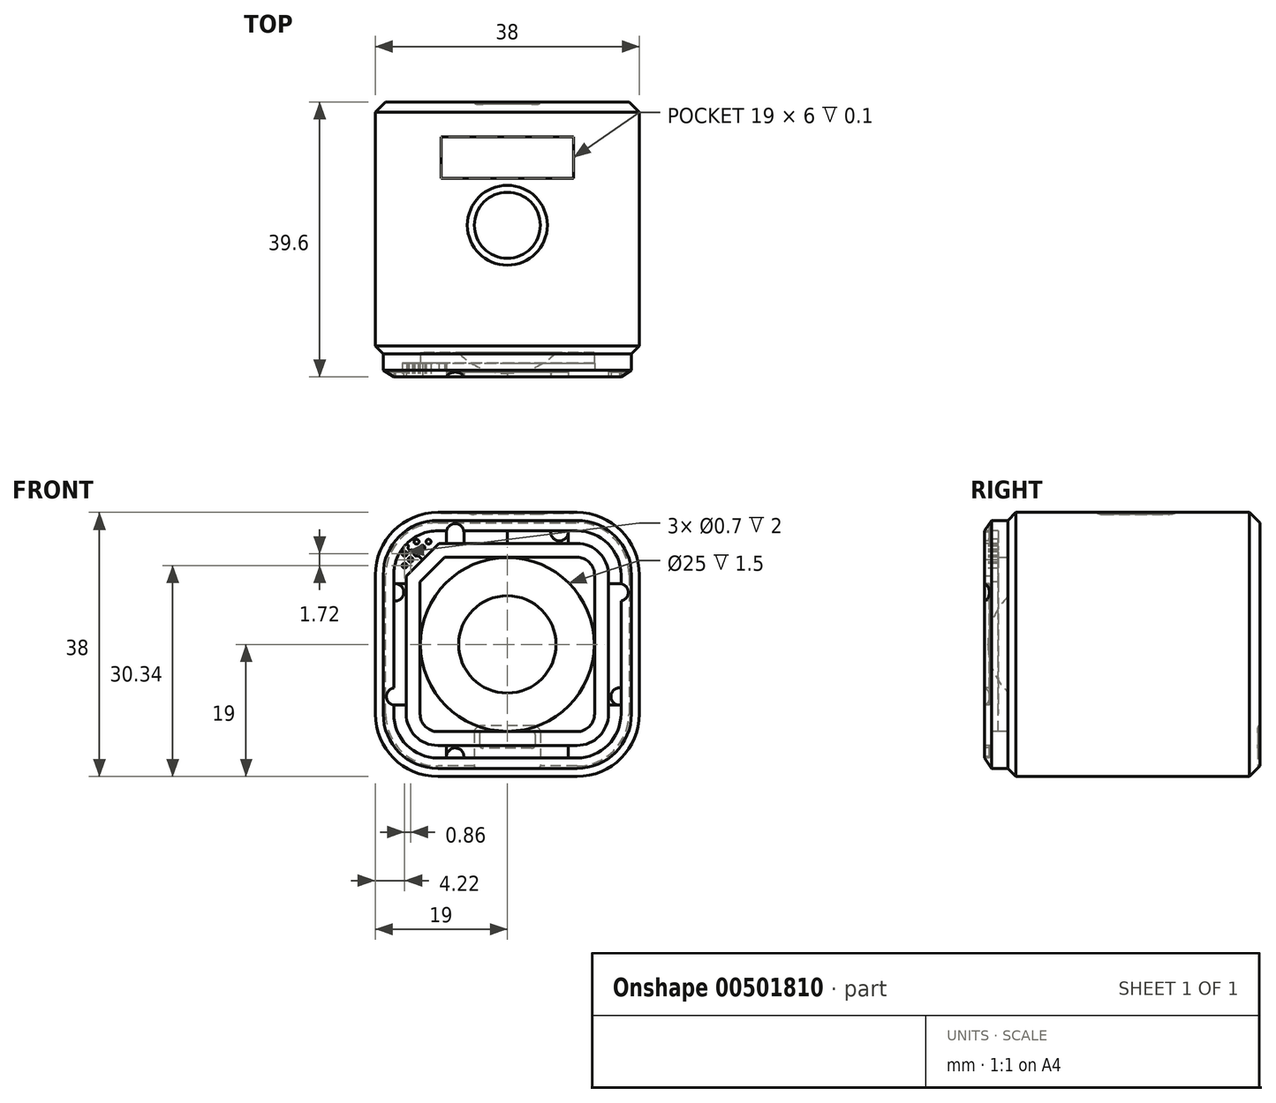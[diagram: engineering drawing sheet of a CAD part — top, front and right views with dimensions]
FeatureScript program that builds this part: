
annotation { "Feature Type Name" : "Feature", "Feature Type Description" : "" }
export const myFeature = defineFeature(function(context is Context, id is Id, definition is map)
    precondition{}
    {
        {
            var Q0;
            Q0=qCreatedBy(makeId("Front.planeOp"),FACE);
            var sketch = newSketch(context, id + "F0", { "sketchPlane" : qUnion([Q0])});
            skLineSegment(sketch, "E0.bottom", {"start": v(19, 19) * mm, "end": v(-19, 19) * mm});
            skLineSegment(sketch, "E0.top", {"start": v(19, -19) * mm, "end": v(-19, -19) * mm});
            skLineSegment(sketch, "E0.left", {"start": v(19, 19) * mm, "end": v(19, -19) * mm});
            skLineSegment(sketch, "E0.right", {"start": v(-19, 19) * mm, "end": v(-19, -19) * mm});
            skPoint(sketch, "E0.middle", {"position": v(0, 0) * mm});
            skLineSegment(sketch, "E1.0", {"start": v(17.85, 17.85) * mm, "end": v(-17.85, 17.85) * mm});
            skLineSegment(sketch, "E1.1", {"start": v(17.85, 17.85) * mm, "end": v(17.85, -17.85) * mm});
            skLineSegment(sketch, "E1.2", {"start": v(17.85, -17.85) * mm, "end": v(-17.85, -17.85) * mm});
            skLineSegment(sketch, "E1.3", {"start": v(-17.85, 17.85) * mm, "end": v(-17.85, -17.85) * mm});
            skSolve(sketch);
        }
        {
            var Q0;
            Q0=makeQuery(id+"F0.imprint","IMPRINT",FACE,{"disambiguationData":[TD([[makeQuery(id+"F0.imprint","IMPRINT",EDGE,{"derivedFrom":sQuery(id+"F0.wireOp",EDGE,"E0.bottom")}),1.0]])]});
            var Q1;
            Q1=makeQuery(id+"F0.imprint","IMPRINT",FACE,{"disambiguationData":[TD([[makeQuery(id+"F0.imprint","IMPRINT",EDGE,{"derivedFrom":sQuery(id+"F0.wireOp",EDGE,"E1.0")}),1.0]])]});
            extrude(context, id + "F1", {"entities" : qUnion([Q0, Q1]), "oppositeDirection" : true, "depth" : 36.6 * mm});
        }
        {
            var Q0;
            Q0=makeQuery(id+"F1.opExtrude","SWEPT_EDGE",EDGE,{"disambiguationData":[OSD([sQuery(id+"F0.wireOp",EDGE,"E0.bottom"),sQuery(id+"F0.wireOp",EDGE,"E0.left")])]});
            var Q1;
            Q1=makeQuery(id+"F1.opExtrude","SWEPT_EDGE",EDGE,{"disambiguationData":[OSD([sQuery(id+"F0.wireOp",EDGE,"E0.bottom"),sQuery(id+"F0.wireOp",EDGE,"E0.right")])]});
            var Q2;
            Q2=makeQuery(id+"F1.opExtrude","SWEPT_EDGE",EDGE,{"disambiguationData":[OSD([sQuery(id+"F0.wireOp",EDGE,"E0.top"),sQuery(id+"F0.wireOp",EDGE,"E0.left")])]});
            var Q3;
            Q3=makeQuery(id+"F1.opExtrude","SWEPT_EDGE",EDGE,{"disambiguationData":[OSD([sQuery(id+"F0.wireOp",EDGE,"E0.top"),sQuery(id+"F0.wireOp",EDGE,"E0.right")])]});
            fillet(context, id + "F2", {"entities" : qUnion([Q0, Q1, Q2, Q3]), "radius" : 9 * mm, "tangentPropagation" : true, "allowEdgeOverflow" : false});
        }
        {
            var Q0;
            Q0=makeQuery(id+"F0.imprint","IMPRINT",FACE,{"disambiguationData":[TD([[makeQuery(id+"F0.imprint","IMPRINT",EDGE,{"derivedFrom":sQuery(id+"F0.wireOp",EDGE,"E1.0")}),1.0]])]});
            extrude(context, id + "F3", {"entities" : qUnion([Q0]), "operationType" : NewBodyOperationType.ADD, "depth" : 3 * mm});
        }
        {
            var Q0;
            Q0=makeQuery(id+"F3.opExtrude","SWEPT_EDGE",EDGE,{"disambiguationData":[OSD([sQuery(id+"F0.wireOp",EDGE,"E1.0"),sQuery(id+"F0.wireOp",EDGE,"E1.1")])]});
            var Q1;
            Q1=makeQuery(id+"F3.opExtrude","SWEPT_EDGE",EDGE,{"disambiguationData":[OSD([sQuery(id+"F0.wireOp",EDGE,"E1.0"),sQuery(id+"F0.wireOp",EDGE,"E1.3")])]});
            var Q2;
            Q2=makeQuery(id+"F3.opExtrude","SWEPT_EDGE",EDGE,{"disambiguationData":[OSD([sQuery(id+"F0.wireOp",EDGE,"E1.2"),sQuery(id+"F0.wireOp",EDGE,"E1.3")])]});
            var Q3;
            Q3=makeQuery(id+"F3.opExtrude","SWEPT_EDGE",EDGE,{"disambiguationData":[OSD([sQuery(id+"F0.wireOp",EDGE,"E1.1"),sQuery(id+"F0.wireOp",EDGE,"E1.2")])]});
            fillet(context, id + "F4", {"entities" : qUnion([Q0, Q1, Q2, Q3]), "radius" : 7.85 * mm, "tangentPropagation" : true, "allowEdgeOverflow" : false});
        }
        {
            var Q0;
            Q0=makeQuery(id+"F1.opExtrude","SWEPT_FACE",FACE,{"disambiguationData":[OSD([sQuery(id+"F0.wireOp",EDGE,"E0.bottom")])]});
            var sketch = newSketch(context, id + "F5", { "sketchPlane" : qUnion([Q0])});
            skCircle(sketch, "E2", {"center": v(0, 18.85) * mm, "radius": 5.75 * mm});
            skCircle(sketch, "E3.0", {"center": v(0, 18.85) * mm, "radius": 4.75 * mm});
            skLineSegment(sketch, "E4.bottom", {"start": v(-9.5, 31.6) * mm, "end": v(9.5, 31.6) * mm});
            skLineSegment(sketch, "E4.top", {"start": v(-9.5, 25.6) * mm, "end": v(9.5, 25.6) * mm});
            skLineSegment(sketch, "E4.left", {"start": v(-9.5, 31.6) * mm, "end": v(-9.5, 25.6) * mm});
            skLineSegment(sketch, "E4.right", {"start": v(9.5, 31.6) * mm, "end": v(9.5, 25.6) * mm});
            skPoint(sketch, "E4.middle", {"position": v(0, 28.6) * mm});
            skSolve(sketch);
        }
        {
            var Q0;
            Q0=makeQuery(id+"F5.imprint","IMPRINT",FACE,{"disambiguationData":[TD([[makeQuery(id+"F5.imprint","IMPRINT",EDGE,{"derivedFrom":sQuery(id+"F5.wireOp",EDGE,"E2")}),1.0]])]});
            extrude(context, id + "F6", {"entities" : qUnion([Q0]), "operationType" : NewBodyOperationType.REMOVE, "oppositeDirection" : true, "depth" : 0.3 * mm});
        }
        {
            var Q0;
            Q0=makeQuery(id+"F6.boolean.opBoolean","COPY",EDGE,{"derivedFrom":makeQuery(id+"F6.opExtrude","CAP_EDGE",EDGE,{"disambiguationData":[OSD([sQuery(id+"F5.wireOp",EDGE,"E3.0")])],"isStart":true})});
            fillet(context, id + "F7", {"entities" : qUnion([Q0]), "radius" : 0.1 * mm, "tangentPropagation" : true, "allowEdgeOverflow" : false});
        }
        {
            var Q0;
            Q0=makeQuery(id+"F5.imprint","IMPRINT",FACE,{"disambiguationData":[TD([[makeQuery(id+"F5.imprint","IMPRINT",EDGE,{"derivedFrom":sQuery(id+"F5.wireOp",EDGE,"E4.bottom")}),-1.0]])]});
            extrude(context, id + "F8", {"entities" : qUnion([Q0]), "operationType" : NewBodyOperationType.REMOVE, "oppositeDirection" : true, "depth" : 0.1 * mm});
        }
        {
            var Q0;
            Q0=makeQuery(id+"F6.boolean.opBoolean","COPY",EDGE,{"derivedFrom":makeQuery(id+"F6.opExtrude","CAP_EDGE",EDGE,{"disambiguationData":[OSD([sQuery(id+"F5.wireOp",EDGE,"E2")])],"isStart":false})});
            fillet(context, id + "F9", {"entities" : qUnion([Q0]), "radius" : 1.7 * mm, "tangentPropagation" : true, "allowEdgeOverflow" : false});
        }
        {
            var Q0;
            Q0=makeQuery(id+"F1.opExtrude","CAP_FACE",FACE,{"disambiguationData":[OSD([sQuery(id+"F0.wireOp",EDGE,"E0.bottom"),sQuery(id+"F0.wireOp",EDGE,"E0.top"),sQuery(id+"F0.wireOp",EDGE,"E0.left"),sQuery(id+"F0.wireOp",EDGE,"E0.right")])],"isStart":false});
            var Q1;
            Q1=makeQuery(id+"F1.opExtrude","CAP_EDGE",EDGE,{"disambiguationData":[OSD([sQuery(id+"F0.wireOp",EDGE,"E0.bottom")])],"isStart":true});
            chamfer(context, id + "F10", {"entities" : qUnion([Q0, Q1]), "width" : 1.5 * mm, "tangentPropagation" : true});
        }
        {
            var Q0;
            Q0=makeQuery(id+"F3.opExtrude","CAP_FACE",FACE,{"disambiguationData":[OSD([sQuery(id+"F0.wireOp",EDGE,"E1.0"),sQuery(id+"F0.wireOp",EDGE,"E1.1"),sQuery(id+"F0.wireOp",EDGE,"E1.2"),sQuery(id+"F0.wireOp",EDGE,"E1.3")])],"isStart":false});
            chamfer(context, id + "F11", {"entities" : qUnion([Q0]), "chamferType" : ChamferType.TWO_OFFSETS, "width1" : 1.5 * mm, "oppositeDirection" : false, "width2" : 1 * mm, "tangentPropagation" : true});
        }
        {
            var Q0;
            Q0=makeQuery(id+"F3.opExtrude","CAP_FACE",FACE,{"disambiguationData":[OSD([sQuery(id+"F0.wireOp",EDGE,"E1.0"),sQuery(id+"F0.wireOp",EDGE,"E1.1"),sQuery(id+"F0.wireOp",EDGE,"E1.2"),sQuery(id+"F0.wireOp",EDGE,"E1.3")])],"isStart":false});
            var sketch = newSketch(context, id + "F12", { "sketchPlane" : qUnion([Q0])});
            skLineSegment(sketch, "E5.1", {"start": v(10, 14.55) * mm, "end": v(-9.85, 14.55) * mm});
            skLineSegment(sketch, "E5.2", {"start": v(-14.55, 9.85) * mm, "end": v(-14.55, -10) * mm});
            skArc(sketch, "E5.3", {"start": v(14.55, 10) * mm, "mid": v(13.22, 13.22) * mm, "end": v(10, 14.55) * mm});
            skArc(sketch, "E5.4", {"start": v(-14.55, -10) * mm, "mid": v(-13.22, -13.22) * mm, "end": v(-10, -14.55) * mm});
            skLineSegment(sketch, "E5.5", {"start": v(-10, -14.55) * mm, "end": v(10, -14.55) * mm});
            skArc(sketch, "E5.6", {"start": v(10, -14.55) * mm, "mid": v(13.22, -13.22) * mm, "end": v(14.55, -10) * mm});
            skLineSegment(sketch, "E5.7", {"start": v(14.55, -10) * mm, "end": v(14.55, 10) * mm});
            skLineSegment(sketch, "E6", {"start": v(-14.55, 9.85) * mm, "end": v(-9.85, 14.55) * mm});
            skCircle(sketch, "E7", {"center": v(-13.06, 13.06) * mm, "radius": 0.35 * mm});
            skLineSegment(sketch, "E8", {"start": v(-12.2, 12.2) * mm, "end": v(-14.5, 14.5) * mm});
            skCircle(sketch, "E9", {"center": v(-13.92, 13.92) * mm, "radius": 0.35 * mm});
            skCircle(sketch, "E10", {"center": v(-13.92, 12.2) * mm, "radius": 0.35 * mm});
            skCircle(sketch, "E11", {"center": v(-14.78, 11.34) * mm, "radius": 0.35 * mm});
            skCircle(sketch, "E12", {"center": v(-14.78, 13.06) * mm, "radius": 0.35 * mm});
            skCircle(sketch, "E13.MirrorC", {"center": v(-12.2, 13.92) * mm, "radius": 0.35 * mm});
            skCircle(sketch, "E14.MirrorC", {"center": v(-13.06, 14.78) * mm, "radius": 0.35 * mm});
            skCircle(sketch, "E15.MirrorC", {"center": v(-11.34, 14.78) * mm, "radius": 0.35 * mm});
            skPoint(sketch, "E16", {"position": v(-7.5, 16.15) * mm});
            skLineSegment(sketch, "E17", {"start": v(0, 16.35) * mm, "end": v(0, 14.55) * mm});
            skCircle(sketch, "E18", {"center": v(-7.5, 16.15) * mm, "radius": 1.25 * mm});
            skLineSegment(sketch, "E19", {"start": v(-8.75, 16.15) * mm, "end": v(-8.75, 14.55) * mm});
            skLineSegment(sketch, "E20", {"start": v(-6.25, 16.15) * mm, "end": v(-6.25, 14.55) * mm});
            skLineSegment(sketch, "E21.MirrorCS", {"start": v(6.25, 16.15) * mm, "end": v(6.25, 14.55) * mm});
            skCircle(sketch, "E22.MirrorC", {"center": v(7.5, 16.15) * mm, "radius": 1.25 * mm});
            skLineSegment(sketch, "E23.MirrorCS", {"start": v(8.75, 16.15) * mm, "end": v(8.75, 14.55) * mm});
            skLineSegment(sketch, "E24.MirrorCS", {"start": v(-6.25, -16.15) * mm, "end": v(-6.25, -14.55) * mm});
            skCircle(sketch, "E25.MirrorC", {"center": v(-7.5, -16.15) * mm, "radius": 1.25 * mm});
            skLineSegment(sketch, "E26.MirrorCS", {"start": v(-8.75, -16.15) * mm, "end": v(-8.75, -14.55) * mm});
            skLineSegment(sketch, "E27.MirrorCS", {"start": v(6.25, -16.15) * mm, "end": v(6.25, -14.55) * mm});
            skCircle(sketch, "E28.MirrorC", {"center": v(7.5, -16.15) * mm, "radius": 1.25 * mm});
            skLineSegment(sketch, "E29.MirrorCS", {"start": v(8.75, -16.15) * mm, "end": v(8.75, -14.55) * mm});
            skLineSegment(sketch, "E30.MirrorCS", {"start": v(-16.15, -8.75) * mm, "end": v(-14.55, -8.75) * mm});
            skCircle(sketch, "E31.MirrorC", {"center": v(-16.15, -7.5) * mm, "radius": 1.25 * mm});
            skLineSegment(sketch, "E32.MirrorCS", {"start": v(-16.15, -6.25) * mm, "end": v(-14.55, -6.25) * mm});
            skLineSegment(sketch, "E33.MirrorCS", {"start": v(-16.15, 6.25) * mm, "end": v(-14.55, 6.25) * mm});
            skCircle(sketch, "E34.MirrorC", {"center": v(-16.15, 7.5) * mm, "radius": 1.25 * mm});
            skLineSegment(sketch, "E35.MirrorCS", {"start": v(-16.15, 8.75) * mm, "end": v(-14.55, 8.75) * mm});
            skLineSegment(sketch, "E36.MirrorCS", {"start": v(16.15, 8.75) * mm, "end": v(14.55, 8.75) * mm});
            skCircle(sketch, "E37.MirrorC", {"center": v(16.15, 7.5) * mm, "radius": 1.25 * mm});
            skLineSegment(sketch, "E38.MirrorCS", {"start": v(16.15, 6.25) * mm, "end": v(14.55, 6.25) * mm});
            skLineSegment(sketch, "E39.MirrorCS", {"start": v(16.15, -6.25) * mm, "end": v(14.55, -6.25) * mm});
            skCircle(sketch, "E40.MirrorC", {"center": v(16.15, -7.5) * mm, "radius": 1.25 * mm});
            skLineSegment(sketch, "E41.MirrorCS", {"start": v(16.15, -8.75) * mm, "end": v(14.55, -8.75) * mm});
            skSolve(sketch);
        }
        {
            var Q0;
            Q0=makeQuery(id+"F12.imprint","IMPRINT",FACE,{"disambiguationData":[TD([[makeQuery(id+"F12.imprint","IMPRINT",EDGE,{"derivedFrom":sQuery(id+"F12.wireOp",EDGE,"E5.1")}),1.0]])]});
            extrude(context, id + "F13", {"entities" : qUnion([Q0]), "operationType" : NewBodyOperationType.REMOVE, "oppositeDirection" : true, "depth" : 1 * mm});
        }
        {
            var Q0;
            Q0=makeQuery(id+"F13.boolean.opBoolean","COPY",FACE,{"derivedFrom":makeQuery(id+"F13.opExtrude","CAP_FACE",FACE,{"disambiguationData":[OSD([sQuery(id+"F12.wireOp",EDGE,"E5.1"),sQuery(id+"F12.wireOp",EDGE,"E5.2"),sQuery(id+"F12.wireOp",EDGE,"E5.3"),sQuery(id+"F12.wireOp",EDGE,"E5.4"),sQuery(id+"F12.wireOp",EDGE,"E5.5"),sQuery(id+"F12.wireOp",EDGE,"E5.6"),sQuery(id+"F12.wireOp",EDGE,"E5.7"),sQuery(id+"F12.wireOp",EDGE,"E6")])],"isStart":false})});
            var sketch = newSketch(context, id + "F14", { "sketchPlane" : qUnion([Q0])});
            skLineSegment(sketch, "E42.0", {"start": v(12.55, -10) * mm, "end": v(12.55, 10) * mm});
            skArc(sketch, "E42.1", {"start": v(10, -12.55) * mm, "mid": v(11.8, -11.8) * mm, "end": v(12.55, -10) * mm});
            skArc(sketch, "E42.2", {"start": v(12.55, 10) * mm, "mid": v(11.8, 11.8) * mm, "end": v(10, 12.55) * mm});
            skLineSegment(sketch, "E42.3", {"start": v(-10, -12.55) * mm, "end": v(10, -12.55) * mm});
            skLineSegment(sketch, "E42.4", {"start": v(10, 12.55) * mm, "end": v(-9.02, 12.55) * mm});
            skLineSegment(sketch, "E42.5", {"start": v(-9.02, 12.55) * mm, "end": v(-12.55, 9.02) * mm});
            skLineSegment(sketch, "E42.6", {"start": v(-12.55, 9.02) * mm, "end": v(-12.55, -10) * mm});
            skArc(sketch, "E42.7", {"start": v(-12.55, -10) * mm, "mid": v(-11.8, -11.8) * mm, "end": v(-10, -12.55) * mm});
            skCircle(sketch, "E43", {"center": v(0, 0) * mm, "radius": 12.5 * mm});
            skPoint(sketch, "E44", {"position": v(0, -12.55) * mm});
            skPoint(sketch, "E45", {"position": v(12.55, 0) * mm});
            skSolve(sketch);
        }
        {
            var Q0;
            Q0=makeQuery(id+"F14.imprint","IMPRINT",FACE,{"disambiguationData":[TD([[makeQuery(id+"F14.imprint","IMPRINT",EDGE,{"derivedFrom":sQuery(id+"F14.wireOp",EDGE,"E42.0")}),1.0]])]});
            extrude(context, id + "F15", {"entities" : qUnion([Q0]), "operationType" : NewBodyOperationType.REMOVE, "oppositeDirection" : true, "depth" : 1 * mm});
        }
        {
            var Q0;
            Q0=makeQuery(id+"F15.boolean.opBoolean","SPLIT",FACE,{"disambiguationData":[TD([makeQuery(id+"F15.opExtrude","SWEPT_FACE",FACE,{"disambiguationData":[OSD([sQuery(id+"F14.wireOp",EDGE,"E43")])]})])],"derivedFrom":makeQuery(id+"F13.boolean.opBoolean","COPY",FACE,{"derivedFrom":makeQuery(id+"F13.opExtrude","CAP_FACE",FACE,{"disambiguationData":[OSD([sQuery(id+"F12.wireOp",EDGE,"E5.1"),sQuery(id+"F12.wireOp",EDGE,"E5.2"),sQuery(id+"F12.wireOp",EDGE,"E5.3"),sQuery(id+"F12.wireOp",EDGE,"E5.4"),sQuery(id+"F12.wireOp",EDGE,"E5.5"),sQuery(id+"F12.wireOp",EDGE,"E5.6"),sQuery(id+"F12.wireOp",EDGE,"E5.7"),sQuery(id+"F12.wireOp",EDGE,"E6")])],"isStart":false})})});
            extrude(context, id + "F16", {"entities" : qUnion([Q0]), "operationType" : NewBodyOperationType.REMOVE, "oppositeDirection" : true, "depth" : 2.5 * mm});
        }
        {
            var Q0;
            Q0=makeQuery(id+"F16.boolean.opBoolean","COPY",FACE,{"derivedFrom":makeQuery(id+"F16.opExtrude","CAP_FACE",FACE,{"disambiguationData":[OSD([sQuery(id+"F12.wireOp",EDGE,"E5.1"),sQuery(id+"F12.wireOp",EDGE,"E5.2"),sQuery(id+"F12.wireOp",EDGE,"E5.3"),sQuery(id+"F12.wireOp",EDGE,"E5.4"),sQuery(id+"F12.wireOp",EDGE,"E5.5"),sQuery(id+"F12.wireOp",EDGE,"E5.6"),sQuery(id+"F12.wireOp",EDGE,"E5.7"),sQuery(id+"F12.wireOp",EDGE,"E6")])],"isStart":false})});
            var sketch = newSketch(context, id + "F17", { "sketchPlane" : qUnion([Q0])});
            skCircle(sketch, "E46.0", {"center": v(0, 0) * mm, "radius": 7 * mm});
            skCircle(sketch, "E47.0", {"center": v(0, 0) * mm, "radius": 17.5 * mm});
            skSolve(sketch);
        }
        {
            var Q0;
            Q0=makeQuery(id+"F17.imprint","IMPRINT",FACE,{"disambiguationData":[TD([[makeQuery(id+"F17.imprint","IMPRINT",EDGE,{"derivedFrom":sQuery(id+"F17.wireOp",EDGE,"E46.0")}),1.0]])]});
            extrude(context, id + "F18", {"entities" : qUnion([Q0]), "operationType" : NewBodyOperationType.ADD, "depth" : 3 * mm});
        }
        {
            var Q0;
            Q0=makeQuery(id+"F18.opExtrude","CAP_EDGE",EDGE,{"disambiguationData":[OSD([sQuery(id+"F17.wireOp",EDGE,"E46.0")])],"isStart":false});
            fillet(context, id + "F19", {"entities" : qUnion([Q0]), "radius" : 9.5 * mm, "tangentPropagation" : true, "allowEdgeOverflow" : false});
        }
        {
            var Q0;
            Q0=makeQuery(id+"F12.imprint","IMPRINT",FACE,{"disambiguationData":[TD([[makeQuery(id+"F12.imprint","IMPRINT",EDGE,{"derivedFrom":sQuery(id+"F12.wireOp",EDGE,"E11")}),1.0]])]});
            var Q1;
            Q1=makeQuery(id+"F12.imprint","IMPRINT",FACE,{"disambiguationData":[TD([[makeQuery(id+"F12.imprint","IMPRINT",EDGE,{"derivedFrom":sQuery(id+"F12.wireOp",EDGE,"E10")}),1.0]])]});
            var Q2;
            Q2=makeQuery(id+"F12.imprint","IMPRINT",FACE,{"disambiguationData":[TD([[makeQuery(id+"F12.imprint","IMPRINT",EDGE,{"derivedFrom":sQuery(id+"F12.wireOp",EDGE,"E12")}),1.0]])]});
            var Q3;
            {var subQ0=sQuery(id+"F12.wireOp",EDGE,"E9");var subQ1=sQuery(id+"F12.wireOp",EDGE,"E8");var subQ2=makeQuery(id+"F12.imprint","INTERSECT",VERTEX,{"disambiguationData":[OD(0.0)],"derivedFrom":[subQ1,subQ0]});Q3=makeQuery(id+"F12.imprint","IMPRINT",FACE,{"disambiguationData":[TD([[makeQuery(id+"F12.imprint","IMPRINT",EDGE,{"disambiguationData":[TD([[subQ2,-1.0]])],"derivedFrom":subQ1}),1.0]])]});}
            var Q4;
            {var subQ0=sQuery(id+"F12.wireOp",EDGE,"E9");var subQ1=sQuery(id+"F12.wireOp",EDGE,"E8");var subQ2=makeQuery(id+"F12.imprint","INTERSECT",VERTEX,{"disambiguationData":[OD(0.0)],"derivedFrom":[subQ1,subQ0]});Q4=makeQuery(id+"F12.imprint","IMPRINT",FACE,{"disambiguationData":[TD([[makeQuery(id+"F12.imprint","IMPRINT",EDGE,{"disambiguationData":[TD([[subQ2,-1.0]])],"derivedFrom":subQ1}),-1.0]])]});}
            var Q5;
            Q5=makeQuery(id+"F12.imprint","IMPRINT",FACE,{"disambiguationData":[TD([[makeQuery(id+"F12.imprint","IMPRINT",EDGE,{"derivedFrom":sQuery(id+"F12.wireOp",EDGE,"E14.MirrorC")}),-1.0]])]});
            var Q6;
            {var subQ0=sQuery(id+"F12.wireOp",EDGE,"E8");var subQ1=sQuery(id+"F12.wireOp",EDGE,"E7");var subQ2=makeQuery(id+"F12.imprint","INTERSECT",VERTEX,{"disambiguationData":[OD(0.0)],"derivedFrom":[subQ1,subQ0]});Q6=makeQuery(id+"F12.imprint","IMPRINT",FACE,{"disambiguationData":[TD([[makeQuery(id+"F12.imprint","IMPRINT",EDGE,{"disambiguationData":[TD([[subQ2,1.0]])],"derivedFrom":subQ1}),1.0]])]});}
            var Q7;
            {var subQ0=sQuery(id+"F12.wireOp",EDGE,"E8");var subQ1=sQuery(id+"F12.wireOp",EDGE,"E7");var subQ2=makeQuery(id+"F12.imprint","INTERSECT",VERTEX,{"disambiguationData":[OD(0.0)],"derivedFrom":[subQ1,subQ0]});Q7=makeQuery(id+"F12.imprint","IMPRINT",FACE,{"disambiguationData":[TD([[makeQuery(id+"F12.imprint","IMPRINT",EDGE,{"disambiguationData":[TD([[subQ2,-1.0]])],"derivedFrom":subQ1}),1.0]])]});}
            var Q8;
            Q8=makeQuery(id+"F12.imprint","IMPRINT",FACE,{"disambiguationData":[TD([[makeQuery(id+"F12.imprint","IMPRINT",EDGE,{"derivedFrom":sQuery(id+"F12.wireOp",EDGE,"E15.MirrorC")}),-1.0]])]});
            var Q9;
            Q9=makeQuery(id+"F12.imprint","IMPRINT",FACE,{"disambiguationData":[TD([[makeQuery(id+"F12.imprint","IMPRINT",EDGE,{"derivedFrom":sQuery(id+"F12.wireOp",EDGE,"E13.MirrorC")}),-1.0]])]});
            extrude(context, id + "F20", {"entities" : qUnion([Q0, Q1, Q2, Q3, Q4, Q5, Q6, Q7, Q8, Q9]), "operationType" : NewBodyOperationType.REMOVE, "oppositeDirection" : true, "depth" : 2 * mm});
        }
        {
            var Q0;
            {var subQ0=sQuery(id+"F12.wireOp",EDGE,"E18");var subQ1=sQuery(id+"F0.wireOp",EDGE,"E1.0");var subQ2=makeQuery(id+"F11.opChamfer","BLEND_EDGE",EDGE,{"blendedFrom":[makeQuery(id+"F3.opExtrude","CAP_EDGE",EDGE,{"disambiguationData":[OSD([subQ1])],"isStart":false}),makeQuery(id+"F3.opExtrude","CAP_FACE",FACE,{"disambiguationData":[OSD([subQ1,sQuery(id+"F0.wireOp",EDGE,"E1.1"),sQuery(id+"F0.wireOp",EDGE,"E1.2"),sQuery(id+"F0.wireOp",EDGE,"E1.3")])],"isStart":false})],"blendedInto":[makeQuery(id+"F3.opExtrude","CAP_FACE",FACE,{"disambiguationData":[OSD([subQ1,sQuery(id+"F0.wireOp",EDGE,"E1.1"),sQuery(id+"F0.wireOp",EDGE,"E1.2"),sQuery(id+"F0.wireOp",EDGE,"E1.3")])],"isStart":false})]});var subQ3=makeQuery(id+"F12.imprint","INTERSECT",VERTEX,{"disambiguationData":[OD(0.0)],"derivedFrom":[subQ2,subQ0]});Q0=makeQuery(id+"F12.imprint","IMPRINT",FACE,{"disambiguationData":[TD([[makeQuery(id+"F12.imprint","IMPRINT",EDGE,{"disambiguationData":[TD([[subQ3,-1.0]])],"derivedFrom":subQ0}),1.0]])]});}
            var Q1;
            {var subQ0=sQuery(id+"F12.wireOp",EDGE,"E18");var subQ5=makeQuery(id+"F12.imprint","INTERSECT",VERTEX,{"derivedFrom":[subQ0,sQuery(id+"F12.wireOp",EDGE,"E19")]});Q1=makeQuery(id+"F12.imprint","IMPRINT",FACE,{"disambiguationData":[TD([[makeQuery(id+"F12.imprint","IMPRINT",EDGE,{"disambiguationData":[TD([[subQ5,-1.0]])],"derivedFrom":subQ0}),1.0]])]});}
            var Q2;
            {var subQ0=sQuery(id+"F12.wireOp",EDGE,"E19");Q2=makeQuery(id+"F12.imprint","IMPRINT",FACE,{"disambiguationData":[TD([[makeQuery(id+"F12.imprint","IMPRINT",EDGE,{"derivedFrom":subQ0}),1.0]])]});}
            var Q3;
            {var subQ0=sQuery(id+"F12.wireOp",EDGE,"E22.MirrorC");var subQ1=sQuery(id+"F0.wireOp",EDGE,"E1.0");var subQ2=makeQuery(id+"F11.opChamfer","BLEND_EDGE",EDGE,{"blendedFrom":[makeQuery(id+"F3.opExtrude","CAP_EDGE",EDGE,{"disambiguationData":[OSD([subQ1])],"isStart":false}),makeQuery(id+"F3.opExtrude","CAP_FACE",FACE,{"disambiguationData":[OSD([subQ1,sQuery(id+"F0.wireOp",EDGE,"E1.1"),sQuery(id+"F0.wireOp",EDGE,"E1.2"),sQuery(id+"F0.wireOp",EDGE,"E1.3")])],"isStart":false})],"blendedInto":[makeQuery(id+"F3.opExtrude","CAP_FACE",FACE,{"disambiguationData":[OSD([subQ1,sQuery(id+"F0.wireOp",EDGE,"E1.1"),sQuery(id+"F0.wireOp",EDGE,"E1.2"),sQuery(id+"F0.wireOp",EDGE,"E1.3")])],"isStart":false})]});var subQ3=makeQuery(id+"F12.imprint","INTERSECT",VERTEX,{"disambiguationData":[OD(0.0)],"derivedFrom":[subQ2,subQ0]});Q3=makeQuery(id+"F12.imprint","IMPRINT",FACE,{"disambiguationData":[TD([[makeQuery(id+"F12.imprint","IMPRINT",EDGE,{"disambiguationData":[TD([[subQ3,-1.0]])],"derivedFrom":subQ0}),-1.0]])]});}
            var Q4;
            {var subQ0=sQuery(id+"F12.wireOp",EDGE,"E22.MirrorC");var subQ1=makeQuery(id+"F12.imprint","INTERSECT",VERTEX,{"derivedFrom":[sQuery(id+"F12.wireOp",EDGE,"E21.MirrorCS"),subQ0]});Q4=makeQuery(id+"F12.imprint","IMPRINT",FACE,{"disambiguationData":[TD([[makeQuery(id+"F12.imprint","IMPRINT",EDGE,{"disambiguationData":[TD([[subQ1,1.0]])],"derivedFrom":subQ0}),-1.0]])]});}
            var Q5;
            {var subQ0=sQuery(id+"F12.wireOp",EDGE,"E21.MirrorCS");Q5=makeQuery(id+"F12.imprint","IMPRINT",FACE,{"disambiguationData":[TD([[makeQuery(id+"F12.imprint","IMPRINT",EDGE,{"derivedFrom":subQ0}),1.0]])]});}
            var Q6;
            {var subQ0=sQuery(id+"F12.wireOp",EDGE,"E36.MirrorCS");Q6=makeQuery(id+"F12.imprint","IMPRINT",FACE,{"disambiguationData":[TD([[makeQuery(id+"F12.imprint","IMPRINT",EDGE,{"derivedFrom":subQ0}),1.0]])]});}
            var Q7;
            {var subQ0=sQuery(id+"F12.wireOp",EDGE,"E37.MirrorC");var subQ5=makeQuery(id+"F12.imprint","INTERSECT",VERTEX,{"derivedFrom":[sQuery(id+"F12.wireOp",EDGE,"E36.MirrorCS"),subQ0]});Q7=makeQuery(id+"F12.imprint","IMPRINT",FACE,{"disambiguationData":[TD([[makeQuery(id+"F12.imprint","IMPRINT",EDGE,{"disambiguationData":[TD([[subQ5,-1.0]])],"derivedFrom":subQ0}),1.0]])]});}
            var Q8;
            {var subQ0=sQuery(id+"F12.wireOp",EDGE,"E37.MirrorC");var subQ1=sQuery(id+"F0.wireOp",EDGE,"E1.1");var subQ2=makeQuery(id+"F11.opChamfer","BLEND_EDGE",EDGE,{"blendedFrom":[makeQuery(id+"F3.opExtrude","CAP_EDGE",EDGE,{"disambiguationData":[OSD([subQ1])],"isStart":false}),makeQuery(id+"F3.opExtrude","CAP_FACE",FACE,{"disambiguationData":[OSD([sQuery(id+"F0.wireOp",EDGE,"E1.0"),subQ1,sQuery(id+"F0.wireOp",EDGE,"E1.2"),sQuery(id+"F0.wireOp",EDGE,"E1.3")])],"isStart":false})],"blendedInto":[makeQuery(id+"F3.opExtrude","CAP_FACE",FACE,{"disambiguationData":[OSD([sQuery(id+"F0.wireOp",EDGE,"E1.0"),subQ1,sQuery(id+"F0.wireOp",EDGE,"E1.2"),sQuery(id+"F0.wireOp",EDGE,"E1.3")])],"isStart":false})]});var subQ3=makeQuery(id+"F12.imprint","INTERSECT",VERTEX,{"disambiguationData":[OD(0.0)],"derivedFrom":[subQ2,subQ0]});Q8=makeQuery(id+"F12.imprint","IMPRINT",FACE,{"disambiguationData":[TD([[makeQuery(id+"F12.imprint","IMPRINT",EDGE,{"disambiguationData":[TD([[subQ3,-1.0]])],"derivedFrom":subQ0}),1.0]])]});}
            var Q9;
            {var subQ0=sQuery(id+"F12.wireOp",EDGE,"E39.MirrorCS");Q9=makeQuery(id+"F12.imprint","IMPRINT",FACE,{"disambiguationData":[TD([[makeQuery(id+"F12.imprint","IMPRINT",EDGE,{"derivedFrom":subQ0}),1.0]])]});}
            var Q10;
            {var subQ0=sQuery(id+"F12.wireOp",EDGE,"E40.MirrorC");var subQ1=makeQuery(id+"F12.imprint","INTERSECT",VERTEX,{"derivedFrom":[sQuery(id+"F12.wireOp",EDGE,"E39.MirrorCS"),subQ0]});Q10=makeQuery(id+"F12.imprint","IMPRINT",FACE,{"disambiguationData":[TD([[makeQuery(id+"F12.imprint","IMPRINT",EDGE,{"disambiguationData":[TD([[subQ1,1.0]])],"derivedFrom":subQ0}),-1.0]])]});}
            var Q11;
            {var subQ0=sQuery(id+"F12.wireOp",EDGE,"E40.MirrorC");var subQ1=sQuery(id+"F0.wireOp",EDGE,"E1.1");var subQ2=makeQuery(id+"F11.opChamfer","BLEND_EDGE",EDGE,{"blendedFrom":[makeQuery(id+"F3.opExtrude","CAP_EDGE",EDGE,{"disambiguationData":[OSD([subQ1])],"isStart":false}),makeQuery(id+"F3.opExtrude","CAP_FACE",FACE,{"disambiguationData":[OSD([sQuery(id+"F0.wireOp",EDGE,"E1.0"),subQ1,sQuery(id+"F0.wireOp",EDGE,"E1.2"),sQuery(id+"F0.wireOp",EDGE,"E1.3")])],"isStart":false})],"blendedInto":[makeQuery(id+"F3.opExtrude","CAP_FACE",FACE,{"disambiguationData":[OSD([sQuery(id+"F0.wireOp",EDGE,"E1.0"),subQ1,sQuery(id+"F0.wireOp",EDGE,"E1.2"),sQuery(id+"F0.wireOp",EDGE,"E1.3")])],"isStart":false})]});var subQ3=makeQuery(id+"F12.imprint","INTERSECT",VERTEX,{"disambiguationData":[OD(0.0)],"derivedFrom":[subQ2,subQ0]});Q11=makeQuery(id+"F12.imprint","IMPRINT",FACE,{"disambiguationData":[TD([[makeQuery(id+"F12.imprint","IMPRINT",EDGE,{"disambiguationData":[TD([[subQ3,-1.0]])],"derivedFrom":subQ0}),-1.0]])]});}
            var Q12;
            {var subQ0=sQuery(id+"F12.wireOp",EDGE,"E27.MirrorCS");Q12=makeQuery(id+"F12.imprint","IMPRINT",FACE,{"disambiguationData":[TD([[makeQuery(id+"F12.imprint","IMPRINT",EDGE,{"derivedFrom":subQ0}),-1.0]])]});}
            var Q13;
            {var subQ0=sQuery(id+"F12.wireOp",EDGE,"E28.MirrorC");var subQ1=makeQuery(id+"F12.imprint","INTERSECT",VERTEX,{"derivedFrom":[sQuery(id+"F12.wireOp",EDGE,"E27.MirrorCS"),subQ0]});Q13=makeQuery(id+"F12.imprint","IMPRINT",FACE,{"disambiguationData":[TD([[makeQuery(id+"F12.imprint","IMPRINT",EDGE,{"disambiguationData":[TD([[subQ1,1.0]])],"derivedFrom":subQ0}),1.0]])]});}
            var Q14;
            {var subQ0=sQuery(id+"F12.wireOp",EDGE,"E28.MirrorC");var subQ1=sQuery(id+"F0.wireOp",EDGE,"E1.2");var subQ2=makeQuery(id+"F11.opChamfer","BLEND_EDGE",EDGE,{"blendedFrom":[makeQuery(id+"F3.opExtrude","CAP_EDGE",EDGE,{"disambiguationData":[OSD([subQ1])],"isStart":false}),makeQuery(id+"F3.opExtrude","CAP_FACE",FACE,{"disambiguationData":[OSD([sQuery(id+"F0.wireOp",EDGE,"E1.0"),sQuery(id+"F0.wireOp",EDGE,"E1.1"),subQ1,sQuery(id+"F0.wireOp",EDGE,"E1.3")])],"isStart":false})],"blendedInto":[makeQuery(id+"F3.opExtrude","CAP_FACE",FACE,{"disambiguationData":[OSD([sQuery(id+"F0.wireOp",EDGE,"E1.0"),sQuery(id+"F0.wireOp",EDGE,"E1.1"),subQ1,sQuery(id+"F0.wireOp",EDGE,"E1.3")])],"isStart":false})]});var subQ3=makeQuery(id+"F12.imprint","INTERSECT",VERTEX,{"disambiguationData":[OD(0.0)],"derivedFrom":[subQ2,subQ0]});Q14=makeQuery(id+"F12.imprint","IMPRINT",FACE,{"disambiguationData":[TD([[makeQuery(id+"F12.imprint","IMPRINT",EDGE,{"disambiguationData":[TD([[subQ3,-1.0]])],"derivedFrom":subQ0}),1.0]])]});}
            var Q15;
            {var subQ0=sQuery(id+"F12.wireOp",EDGE,"E24.MirrorCS");Q15=makeQuery(id+"F12.imprint","IMPRINT",FACE,{"disambiguationData":[TD([[makeQuery(id+"F12.imprint","IMPRINT",EDGE,{"derivedFrom":subQ0}),1.0]])]});}
            var Q16;
            {var subQ0=sQuery(id+"F12.wireOp",EDGE,"E25.MirrorC");var subQ1=makeQuery(id+"F12.imprint","INTERSECT",VERTEX,{"derivedFrom":[sQuery(id+"F12.wireOp",EDGE,"E24.MirrorCS"),subQ0]});Q16=makeQuery(id+"F12.imprint","IMPRINT",FACE,{"disambiguationData":[TD([[makeQuery(id+"F12.imprint","IMPRINT",EDGE,{"disambiguationData":[TD([[subQ1,1.0]])],"derivedFrom":subQ0}),-1.0]])]});}
            var Q17;
            {var subQ0=sQuery(id+"F12.wireOp",EDGE,"E25.MirrorC");var subQ1=sQuery(id+"F0.wireOp",EDGE,"E1.2");var subQ2=makeQuery(id+"F11.opChamfer","BLEND_EDGE",EDGE,{"blendedFrom":[makeQuery(id+"F3.opExtrude","CAP_EDGE",EDGE,{"disambiguationData":[OSD([subQ1])],"isStart":false}),makeQuery(id+"F3.opExtrude","CAP_FACE",FACE,{"disambiguationData":[OSD([sQuery(id+"F0.wireOp",EDGE,"E1.0"),sQuery(id+"F0.wireOp",EDGE,"E1.1"),subQ1,sQuery(id+"F0.wireOp",EDGE,"E1.3")])],"isStart":false})],"blendedInto":[makeQuery(id+"F3.opExtrude","CAP_FACE",FACE,{"disambiguationData":[OSD([sQuery(id+"F0.wireOp",EDGE,"E1.0"),sQuery(id+"F0.wireOp",EDGE,"E1.1"),subQ1,sQuery(id+"F0.wireOp",EDGE,"E1.3")])],"isStart":false})]});var subQ3=makeQuery(id+"F12.imprint","INTERSECT",VERTEX,{"disambiguationData":[OD(0.0)],"derivedFrom":[subQ2,subQ0]});Q17=makeQuery(id+"F12.imprint","IMPRINT",FACE,{"disambiguationData":[TD([[makeQuery(id+"F12.imprint","IMPRINT",EDGE,{"disambiguationData":[TD([[subQ3,-1.0]])],"derivedFrom":subQ0}),-1.0]])]});}
            var Q18;
            {var subQ0=sQuery(id+"F12.wireOp",EDGE,"E34.MirrorC");var subQ1=sQuery(id+"F0.wireOp",EDGE,"E1.3");var subQ2=makeQuery(id+"F11.opChamfer","BLEND_EDGE",EDGE,{"blendedFrom":[makeQuery(id+"F3.opExtrude","CAP_EDGE",EDGE,{"disambiguationData":[OSD([subQ1])],"isStart":false}),makeQuery(id+"F3.opExtrude","CAP_FACE",FACE,{"disambiguationData":[OSD([sQuery(id+"F0.wireOp",EDGE,"E1.0"),sQuery(id+"F0.wireOp",EDGE,"E1.1"),sQuery(id+"F0.wireOp",EDGE,"E1.2"),subQ1])],"isStart":false})],"blendedInto":[makeQuery(id+"F3.opExtrude","CAP_FACE",FACE,{"disambiguationData":[OSD([sQuery(id+"F0.wireOp",EDGE,"E1.0"),sQuery(id+"F0.wireOp",EDGE,"E1.1"),sQuery(id+"F0.wireOp",EDGE,"E1.2"),subQ1])],"isStart":false})]});var subQ3=makeQuery(id+"F12.imprint","INTERSECT",VERTEX,{"disambiguationData":[OD(0.0)],"derivedFrom":[subQ2,subQ0]});Q18=makeQuery(id+"F12.imprint","IMPRINT",FACE,{"disambiguationData":[TD([[makeQuery(id+"F12.imprint","IMPRINT",EDGE,{"disambiguationData":[TD([[subQ3,-1.0]])],"derivedFrom":subQ0}),-1.0]])]});}
            var Q19;
            {var subQ0=sQuery(id+"F12.wireOp",EDGE,"E34.MirrorC");var subQ1=makeQuery(id+"F12.imprint","INTERSECT",VERTEX,{"derivedFrom":[sQuery(id+"F12.wireOp",EDGE,"E33.MirrorCS"),subQ0]});Q19=makeQuery(id+"F12.imprint","IMPRINT",FACE,{"disambiguationData":[TD([[makeQuery(id+"F12.imprint","IMPRINT",EDGE,{"disambiguationData":[TD([[subQ1,1.0]])],"derivedFrom":subQ0}),-1.0]])]});}
            var Q20;
            {var subQ0=sQuery(id+"F12.wireOp",EDGE,"E33.MirrorCS");Q20=makeQuery(id+"F12.imprint","IMPRINT",FACE,{"disambiguationData":[TD([[makeQuery(id+"F12.imprint","IMPRINT",EDGE,{"derivedFrom":subQ0}),1.0]])]});}
            var Q21;
            {var subQ0=sQuery(id+"F12.wireOp",EDGE,"E31.MirrorC");var subQ1=sQuery(id+"F0.wireOp",EDGE,"E1.3");var subQ2=makeQuery(id+"F11.opChamfer","BLEND_EDGE",EDGE,{"blendedFrom":[makeQuery(id+"F3.opExtrude","CAP_EDGE",EDGE,{"disambiguationData":[OSD([subQ1])],"isStart":false}),makeQuery(id+"F3.opExtrude","CAP_FACE",FACE,{"disambiguationData":[OSD([sQuery(id+"F0.wireOp",EDGE,"E1.0"),sQuery(id+"F0.wireOp",EDGE,"E1.1"),sQuery(id+"F0.wireOp",EDGE,"E1.2"),subQ1])],"isStart":false})],"blendedInto":[makeQuery(id+"F3.opExtrude","CAP_FACE",FACE,{"disambiguationData":[OSD([sQuery(id+"F0.wireOp",EDGE,"E1.0"),sQuery(id+"F0.wireOp",EDGE,"E1.1"),sQuery(id+"F0.wireOp",EDGE,"E1.2"),subQ1])],"isStart":false})]});var subQ3=makeQuery(id+"F12.imprint","INTERSECT",VERTEX,{"disambiguationData":[OD(0.0)],"derivedFrom":[subQ2,subQ0]});Q21=makeQuery(id+"F12.imprint","IMPRINT",FACE,{"disambiguationData":[TD([[makeQuery(id+"F12.imprint","IMPRINT",EDGE,{"disambiguationData":[TD([[subQ3,-1.0]])],"derivedFrom":subQ0}),1.0]])]});}
            var Q22;
            {var subQ0=sQuery(id+"F12.wireOp",EDGE,"E31.MirrorC");var subQ5=makeQuery(id+"F12.imprint","INTERSECT",VERTEX,{"derivedFrom":[sQuery(id+"F12.wireOp",EDGE,"E30.MirrorCS"),subQ0]});Q22=makeQuery(id+"F12.imprint","IMPRINT",FACE,{"disambiguationData":[TD([[makeQuery(id+"F12.imprint","IMPRINT",EDGE,{"disambiguationData":[TD([[subQ5,-1.0]])],"derivedFrom":subQ0}),1.0]])]});}
            var Q23;
            {var subQ0=sQuery(id+"F12.wireOp",EDGE,"E30.MirrorCS");Q23=makeQuery(id+"F12.imprint","IMPRINT",FACE,{"disambiguationData":[TD([[makeQuery(id+"F12.imprint","IMPRINT",EDGE,{"derivedFrom":subQ0}),1.0]])]});}
            extrude(context, id + "F21", {"entities" : qUnion([Q0, Q1, Q2, Q3, Q4, Q5, Q6, Q7, Q8, Q9, Q10, Q11, Q12, Q13, Q14, Q15, Q16, Q17, Q18, Q19, Q20, Q21, Q22, Q23]), "operationType" : NewBodyOperationType.REMOVE, "oppositeDirection" : true, "depth" : 0.7 * mm});
        }
        {
            var Q0;
            Q0=makeQuery(id+"F1.opExtrude","CAP_FACE",FACE,{"disambiguationData":[OSD([sQuery(id+"F0.wireOp",EDGE,"E0.bottom"),sQuery(id+"F0.wireOp",EDGE,"E0.top"),sQuery(id+"F0.wireOp",EDGE,"E0.left"),sQuery(id+"F0.wireOp",EDGE,"E0.right")])],"isStart":false});
            var sketch = newSketch(context, id + "F22", { "sketchPlane" : qUnion([Q0])});
            skLineSegment(sketch, "E48.bottom", {"start": v(-4.75, -11.7) * mm, "end": v(4.75, -11.7) * mm});
            skLineSegment(sketch, "E48.top", {"start": v(-4.75, -18.7) * mm, "end": v(4.75, -18.7) * mm});
            skLineSegment(sketch, "E48.left", {"start": v(-4.75, -11.7) * mm, "end": v(-4.75, -18.7) * mm});
            skLineSegment(sketch, "E48.right", {"start": v(4.75, -11.7) * mm, "end": v(4.75, -18.7) * mm});
            skLineSegment(sketch, "E49.bottom", {"start": v(-4, -12.45) * mm, "end": v(4, -12.45) * mm});
            skLineSegment(sketch, "E49.top", {"start": v(-4, -14.95) * mm, "end": v(4, -14.95) * mm});
            skLineSegment(sketch, "E49.left", {"start": v(-4, -12.45) * mm, "end": v(-4, -14.95) * mm});
            skLineSegment(sketch, "E49.right", {"start": v(4, -12.45) * mm, "end": v(4, -14.95) * mm});
            skSolve(sketch);
        }
        {
            var Q0;
            {var subQ1=sQuery(id+"F22.wireOp",EDGE,"E48.bottom");Q0=makeQuery(id+"F22.imprint","IMPRINT",FACE,{"disambiguationData":[TD([[makeQuery(id+"F22.imprint","IMPRINT",EDGE,{"derivedFrom":subQ1}),-1.0]])]});}
            var Q1;
            {var subQ0=sQuery(id+"F22.wireOp",EDGE,"E48.top");Q1=makeQuery(id+"F22.imprint","IMPRINT",FACE,{"disambiguationData":[TD([[makeQuery(id+"F22.imprint","IMPRINT",EDGE,{"derivedFrom":subQ0}),1.0]])]});}
            extrude(context, id + "F23", {"entities" : qUnion([Q0, Q1]), "operationType" : NewBodyOperationType.REMOVE, "oppositeDirection" : true, "depth" : 0.3 * mm});
        }
        {
            var Q0;
            Q0=makeQuery(id+"F23.boolean.opBoolean","COPY",EDGE,{"derivedFrom":makeQuery(id+"F23.opExtrude","SWEPT_EDGE",EDGE,{"disambiguationData":[OSD([sQuery(id+"F22.wireOp",EDGE,"E48.bottom"),sQuery(id+"F22.wireOp",EDGE,"E48.left")])]})});
            var Q1;
            Q1=makeQuery(id+"F23.boolean.opBoolean","COPY",EDGE,{"derivedFrom":makeQuery(id+"F23.opExtrude","SWEPT_EDGE",EDGE,{"disambiguationData":[OSD([sQuery(id+"F22.wireOp",EDGE,"E48.bottom"),sQuery(id+"F22.wireOp",EDGE,"E48.right")])]})});
            fillet(context, id + "F24", {"entities" : qUnion([Q0, Q1]), "radius" : 1 * mm, "tangentPropagation" : true, "allowEdgeOverflow" : false});
        }
        {
            var Q0;
            Q0=makeQuery(id+"F23.boolean.opBoolean","COPY",EDGE,{"derivedFrom":makeQuery(id+"F23.opExtrude","SWEPT_EDGE",EDGE,{"disambiguationData":[OSD([sQuery(id+"F22.wireOp",EDGE,"E49.top"),sQuery(id+"F22.wireOp",EDGE,"E49.left")])]})});
            var Q1;
            Q1=makeQuery(id+"F23.boolean.opBoolean","COPY",EDGE,{"derivedFrom":makeQuery(id+"F23.opExtrude","SWEPT_EDGE",EDGE,{"disambiguationData":[OSD([sQuery(id+"F22.wireOp",EDGE,"E49.bottom"),sQuery(id+"F22.wireOp",EDGE,"E49.left")])]})});
            var Q2;
            Q2=makeQuery(id+"F23.boolean.opBoolean","COPY",EDGE,{"derivedFrom":makeQuery(id+"F23.opExtrude","SWEPT_EDGE",EDGE,{"disambiguationData":[OSD([sQuery(id+"F22.wireOp",EDGE,"E49.top"),sQuery(id+"F22.wireOp",EDGE,"E49.right")])]})});
            var Q3;
            Q3=makeQuery(id+"F23.boolean.opBoolean","COPY",EDGE,{"derivedFrom":makeQuery(id+"F23.opExtrude","SWEPT_EDGE",EDGE,{"disambiguationData":[OSD([sQuery(id+"F22.wireOp",EDGE,"E49.bottom"),sQuery(id+"F22.wireOp",EDGE,"E49.right")])]})});
            fillet(context, id + "F25", {"entities" : qUnion([Q0, Q1, Q2, Q3]), "radius" : 0.5 * mm, "tangentPropagation" : true, "allowEdgeOverflow" : false});
        }
        {
            var Q0;
            Q0=makeQuery(id+"F23.boolean.opBoolean","COPY",EDGE,{"derivedFrom":makeQuery(id+"F23.opExtrude","CAP_EDGE",EDGE,{"disambiguationData":[OSD([sQuery(id+"F22.wireOp",EDGE,"E48.left")])],"isStart":false})});
            var Q1;
            {var subQ0=sQuery(id+"F22.wireOp",EDGE,"E48.left");var subQ1=sQuery(id+"F22.wireOp",EDGE,"E48.bottom");Q1=makeQuery(id+"F24.opFillet","BLEND_EDGE",EDGE,{"blendedFrom":[makeQuery(id+"F23.boolean.opBoolean","COPY",EDGE,{"derivedFrom":makeQuery(id+"F23.opExtrude","SWEPT_EDGE",EDGE,{"disambiguationData":[OSD([subQ1,subQ0])]})}),makeQuery(id+"F23.boolean.opBoolean","COPY",FACE,{"derivedFrom":makeQuery(id+"F23.opExtrude","CAP_FACE",FACE,{"disambiguationData":[OSD([subQ1,sQuery(id+"F22.wireOp",EDGE,"E48.top"),subQ0,sQuery(id+"F22.wireOp",EDGE,"E48.right"),sQuery(id+"F22.wireOp",EDGE,"E49.bottom"),sQuery(id+"F22.wireOp",EDGE,"E49.top"),sQuery(id+"F22.wireOp",EDGE,"E49.left"),sQuery(id+"F22.wireOp",EDGE,"E49.right")])],"isStart":false})})],"blendedInto":[makeQuery(id+"F23.boolean.opBoolean","COPY",FACE,{"derivedFrom":makeQuery(id+"F23.opExtrude","CAP_FACE",FACE,{"disambiguationData":[OSD([subQ1,sQuery(id+"F22.wireOp",EDGE,"E48.top"),subQ0,sQuery(id+"F22.wireOp",EDGE,"E48.right"),sQuery(id+"F22.wireOp",EDGE,"E49.bottom"),sQuery(id+"F22.wireOp",EDGE,"E49.top"),sQuery(id+"F22.wireOp",EDGE,"E49.left"),sQuery(id+"F22.wireOp",EDGE,"E49.right")])],"isStart":false})})]});}
            var Q2;
            Q2=makeQuery(id+"F23.boolean.opBoolean","COPY",EDGE,{"derivedFrom":makeQuery(id+"F23.opExtrude","CAP_EDGE",EDGE,{"disambiguationData":[OSD([sQuery(id+"F22.wireOp",EDGE,"E48.bottom")])],"isStart":false})});
            var Q3;
            {var subQ0=sQuery(id+"F22.wireOp",EDGE,"E48.right");var subQ1=sQuery(id+"F22.wireOp",EDGE,"E48.bottom");Q3=makeQuery(id+"F24.opFillet","BLEND_EDGE",EDGE,{"blendedFrom":[makeQuery(id+"F23.boolean.opBoolean","COPY",EDGE,{"derivedFrom":makeQuery(id+"F23.opExtrude","SWEPT_EDGE",EDGE,{"disambiguationData":[OSD([subQ1,subQ0])]})}),makeQuery(id+"F23.boolean.opBoolean","COPY",FACE,{"derivedFrom":makeQuery(id+"F23.opExtrude","CAP_FACE",FACE,{"disambiguationData":[OSD([subQ1,sQuery(id+"F22.wireOp",EDGE,"E48.top"),sQuery(id+"F22.wireOp",EDGE,"E48.left"),subQ0,sQuery(id+"F22.wireOp",EDGE,"E49.bottom"),sQuery(id+"F22.wireOp",EDGE,"E49.top"),sQuery(id+"F22.wireOp",EDGE,"E49.left"),sQuery(id+"F22.wireOp",EDGE,"E49.right")])],"isStart":false})})],"blendedInto":[makeQuery(id+"F23.boolean.opBoolean","COPY",FACE,{"derivedFrom":makeQuery(id+"F23.opExtrude","CAP_FACE",FACE,{"disambiguationData":[OSD([subQ1,sQuery(id+"F22.wireOp",EDGE,"E48.top"),sQuery(id+"F22.wireOp",EDGE,"E48.left"),subQ0,sQuery(id+"F22.wireOp",EDGE,"E49.bottom"),sQuery(id+"F22.wireOp",EDGE,"E49.top"),sQuery(id+"F22.wireOp",EDGE,"E49.left"),sQuery(id+"F22.wireOp",EDGE,"E49.right")])],"isStart":false})})]});}
            var Q4;
            Q4=makeQuery(id+"F23.boolean.opBoolean","COPY",EDGE,{"derivedFrom":makeQuery(id+"F23.opExtrude","CAP_EDGE",EDGE,{"disambiguationData":[OSD([sQuery(id+"F22.wireOp",EDGE,"E48.right")])],"isStart":false})});
            fillet(context, id + "F26", {"entities" : qUnion([Q0, Q1, Q2, Q3, Q4]), "radius" : 0.3 * mm, "tangentPropagation" : true, "allowEdgeOverflow" : false});
        }
        {
            var Q0;
            Q0=makeQuery(id+"F1.opExtrude","SWEPT_BODY",BODY,{"disambiguationData":[OSD([sQuery(id+"F0.wireOp",EDGE,"E0.bottom"),sQuery(id+"F0.wireOp",EDGE,"E0.top"),sQuery(id+"F0.wireOp",EDGE,"E0.left"),sQuery(id+"F0.wireOp",EDGE,"E0.right")])]});
            transform(context, id + "F27", {"entities" : qUnion([Q0]), "transformType" : TransformType.TRANSLATION_3D, "dx" : 0 * mm, "dy" : 0 * mm, "dz" : 0 * mm, "makeCopy" : true});
        }
        {
            var Q0;
            Q0=makeQuery(id+"F27.opPattern","COPY",BODY,{"derivedFrom":makeQuery(id+"F1.opExtrude","SWEPT_BODY",BODY,{"disambiguationData":[OSD([sQuery(id+"F0.wireOp",EDGE,"E0.bottom"),sQuery(id+"F0.wireOp",EDGE,"E0.top"),sQuery(id+"F0.wireOp",EDGE,"E0.left"),sQuery(id+"F0.wireOp",EDGE,"E0.right")])]}),"instanceName":"1"});
            transform(context, id + "F28", {"entities" : qUnion([Q0]), "transformType" : TransformType.TRANSLATION_3D, "dx" : 0 * mm, "dy" : 0 * mm, "dz" : 0 * mm, "makeCopy" : true});
        }
        {
            var Q0;
            Q0=makeQuery(id+"F28.opPattern","COPY",BODY,{"derivedFrom":makeQuery(id+"F27.opPattern","COPY",BODY,{"derivedFrom":makeQuery(id+"F1.opExtrude","SWEPT_BODY",BODY,{"disambiguationData":[OSD([sQuery(id+"F0.wireOp",EDGE,"E0.bottom"),sQuery(id+"F0.wireOp",EDGE,"E0.top"),sQuery(id+"F0.wireOp",EDGE,"E0.left"),sQuery(id+"F0.wireOp",EDGE,"E0.right")])]}),"instanceName":"1"}),"instanceName":"1"});
            var Q1;
            Q1=makeQuery(id+"F27.opPattern","COPY",BODY,{"derivedFrom":makeQuery(id+"F1.opExtrude","SWEPT_BODY",BODY,{"disambiguationData":[OSD([sQuery(id+"F0.wireOp",EDGE,"E0.bottom"),sQuery(id+"F0.wireOp",EDGE,"E0.top"),sQuery(id+"F0.wireOp",EDGE,"E0.left"),sQuery(id+"F0.wireOp",EDGE,"E0.right")])]}),"instanceName":"1"});
            deleteBodies(context, id + "F29", {"entities" : qUnion([Q0, Q1])});
        }
    });
